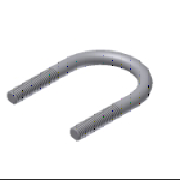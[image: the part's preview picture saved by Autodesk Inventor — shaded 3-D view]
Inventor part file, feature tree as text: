
AUTODESK INVENTOR PART (.ipt)
format: ipt  version: 2023 (Build 270158000, 158)  size: 123,392 bytes
history: native  units: mm
features: sketch x2, plane x1, sweep x1
ambient origin geometry x8: Origin, YZ Plane, XZ Plane, XY Plane, X Axis, Y Axis, Z Axis, Center Point
bodies: Solid1 (feature_tree)
feature tree (4):
  sketch  "Sketch1"  dims[d0=48.0mm d1=152.0mm]
  plane  "Work Plane1"
  sweep  "Колебание1"
  sketch  "Sketch2"  dims[d2=8.0mm d3=0.0mm d4=60.0mm d5=0.0mm d8=1.0mm d9=2.0mm d10=45.0deg d11=60.0mm d12=0.0mm d13=0.0mm]
